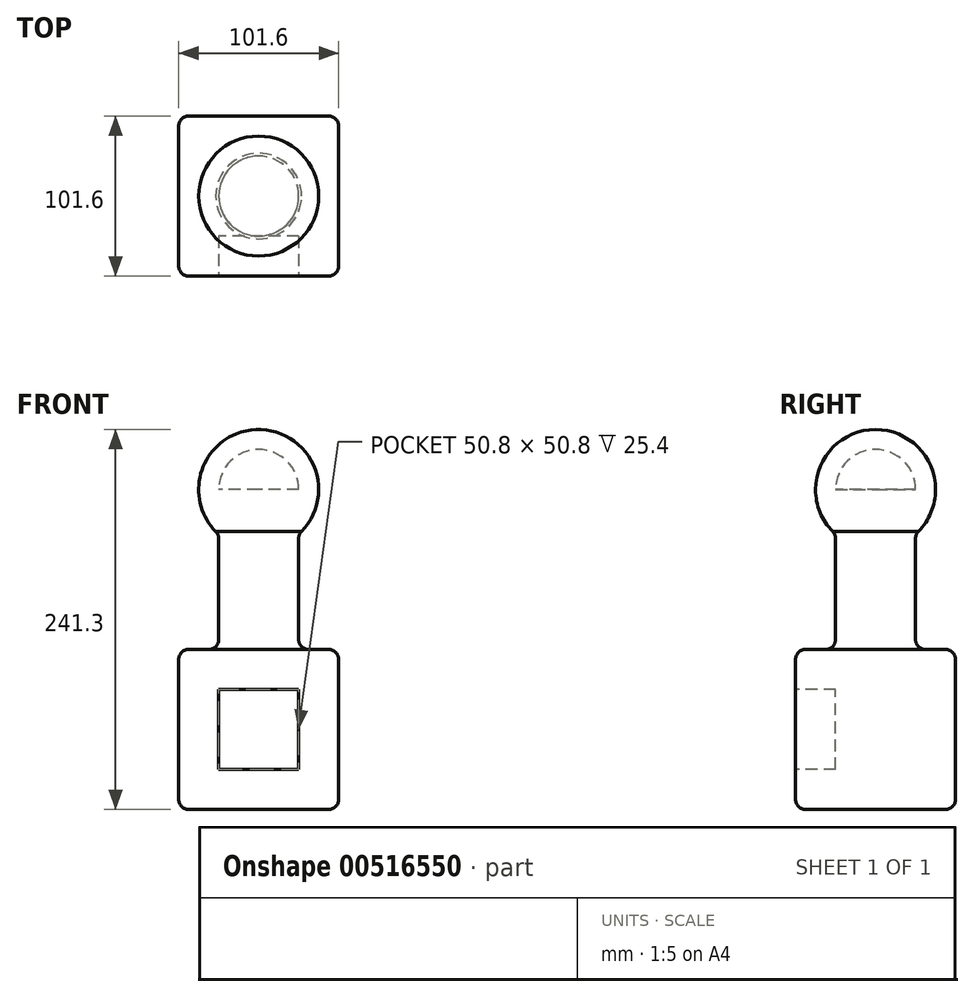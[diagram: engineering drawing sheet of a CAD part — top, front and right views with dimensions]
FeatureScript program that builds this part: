
annotation { "Feature Type Name" : "Feature", "Feature Type Description" : "" }
export const myFeature = defineFeature(function(context is Context, id is Id, definition is map)
    precondition{}
    {
        {
            var Q0;
            Q0=qCreatedBy(makeId("Top.planeOp"),FACE);
            var sketch = newSketch(context, id + "F0", { "sketchPlane" : qUnion([Q0])});
            skLineSegment(sketch, "E0.bottom", {"start": v(-50.8, 50.8) * mm, "end": v(50.8, 50.8) * mm});
            skLineSegment(sketch, "E0.top", {"start": v(-50.8, -50.8) * mm, "end": v(50.8, -50.8) * mm});
            skLineSegment(sketch, "E0.left", {"start": v(-50.8, 50.8) * mm, "end": v(-50.8, -50.8) * mm});
            skLineSegment(sketch, "E0.right", {"start": v(50.8, 50.8) * mm, "end": v(50.8, -50.8) * mm});
            skPoint(sketch, "E0.middle", {"position": v(0, 0) * mm});
            skSolve(sketch);
        }
        {
            var Q0;
            Q0=makeQuery(id+"F0.imprint","IMPRINT",FACE,{"disambiguationData":[TD([[makeQuery(id+"F0.imprint","IMPRINT",EDGE,{"derivedFrom":sQuery(id+"F0.wireOp",EDGE,"E0.bottom")}),-1.0]])]});
            extrude(context, id + "F1", {"entities" : qUnion([Q0]), "depth" : 101.6 * mm, "offsetDistance" : 25.4 * mm});
        }
        {
            var Q0;
            Q0=makeQuery(id+"F1.opExtrude","CAP_FACE",FACE,{"disambiguationData":[OSD([sQuery(id+"F0.wireOp",EDGE,"E0.bottom"),sQuery(id+"F0.wireOp",EDGE,"E0.top"),sQuery(id+"F0.wireOp",EDGE,"E0.left"),sQuery(id+"F0.wireOp",EDGE,"E0.right")])],"isStart":false});
            var sketch = newSketch(context, id + "F2", { "sketchPlane" : qUnion([Q0])});
            skCircle(sketch, "E1", {"center": v(0, 0) * mm, "radius": 25.4 * mm});
            skSolve(sketch);
        }
        {
            var Q0;
            Q0 = qSketchRegion(id + "F2", true);
            extrude(context, id + "F3", {"entities" : qUnion([Q0]), "operationType" : NewBodyOperationType.ADD, "depth" : 101.6 * mm, "offsetDistance" : 25.4 * mm});
        }
        {
            var Q0;
            Q0=makeQuery(id+"F1.opExtrude","SWEPT_FACE",FACE,{"disambiguationData":[OSD([sQuery(id+"F0.wireOp",EDGE,"E0.top")])]});
            var sketch = newSketch(context, id + "F4", { "sketchPlane" : qUnion([Q0])});
            skLineSegment(sketch, "E2.bottom", {"start": v(25.4, 25.4) * mm, "end": v(-25.4, 25.4) * mm});
            skLineSegment(sketch, "E2.top", {"start": v(25.4, 76.2) * mm, "end": v(-25.4, 76.2) * mm});
            skLineSegment(sketch, "E2.left", {"start": v(25.4, 25.4) * mm, "end": v(25.4, 76.2) * mm});
            skLineSegment(sketch, "E2.right", {"start": v(-25.4, 25.4) * mm, "end": v(-25.4, 76.2) * mm});
            skPoint(sketch, "E2.middle", {"position": v(0, 50.8) * mm});
            skPoint(sketch, "E2.middle.positionSnap0", {"position": v(50.8, 50.8) * mm});
            skPoint(sketch, "E2.centerSnap0", {"position": v(50.8, 50.8) * mm});
            skSolve(sketch);
        }
        {
            var Q0;
            Q0=makeQuery(id+"F4.imprint","IMPRINT",FACE,{"disambiguationData":[TD([[makeQuery(id+"F4.imprint","IMPRINT",EDGE,{"derivedFrom":sQuery(id+"F4.wireOp",EDGE,"E2.bottom")}),-1.0]])]});
            extrude(context, id + "F5", {"entities" : qUnion([Q0]), "operationType" : NewBodyOperationType.REMOVE, "oppositeDirection" : true, "depth" : 25.4 * mm, "offsetDistance" : 25.4 * mm});
        }
        {
            var Q0;
            Q0=makeQuery(id+"F3.opExtrude","CAP_FACE",FACE,{"disambiguationData":[OSD([sQuery(id+"F2.wireOp",EDGE,"E1")])],"isStart":false});
            var sketch = newSketch(context, id + "F6", { "sketchPlane" : qUnion([Q0])});
            skArc(sketch, "E3", {"start": v(0, -38.1) * mm, "mid": v(38.1, 0) * mm, "end": v(0, 38.1) * mm});
            skLineSegment(sketch, "E4", {"start": v(0, 38.1) * mm, "end": v(0, -38.1) * mm});
            skSolve(sketch);
        }
        {
            var Q0;
            {var subQ0=sQuery(id+"F6.wireOp",EDGE,"E3");Q0=makeQuery(id+"F6.imprint","IMPRINT",FACE,{"disambiguationData":[TD([[makeQuery(id+"F6.imprint","IMPRINT",EDGE,{"derivedFrom":subQ0}),1.0]])]});}
            var Q1;
            Q1=sQuery(id+"F6.wireOp",EDGE,"E4");
            revolve(context, id + "F7", {"operationType" : NewBodyOperationType.ADD, "entities" : qUnion([Q0]), "axis" : qUnion([Q1]), "revolveType" : RevolveType.FULL});
        }
        {
            var Q0;
            Q0=makeQuery(id+"F1.opExtrude","CAP_EDGE",EDGE,{"disambiguationData":[OSD([sQuery(id+"F0.wireOp",EDGE,"E0.top")])],"isStart":false});
            var Q1;
            Q1=makeQuery(id+"F1.opExtrude","CAP_EDGE",EDGE,{"disambiguationData":[OSD([sQuery(id+"F0.wireOp",EDGE,"E0.left")])],"isStart":false});
            var Q2;
            Q2=makeQuery(id+"F1.opExtrude","CAP_EDGE",EDGE,{"disambiguationData":[OSD([sQuery(id+"F0.wireOp",EDGE,"E0.bottom")])],"isStart":false});
            var Q3;
            Q3=makeQuery(id+"F1.opExtrude","CAP_EDGE",EDGE,{"disambiguationData":[OSD([sQuery(id+"F0.wireOp",EDGE,"E0.right")])],"isStart":false});
            var Q4;
            Q4=makeQuery(id+"F1.opExtrude","SWEPT_EDGE",EDGE,{"disambiguationData":[OSD([sQuery(id+"F0.wireOp",EDGE,"E0.top"),sQuery(id+"F0.wireOp",EDGE,"E0.right")])]});
            var Q5;
            Q5=makeQuery(id+"F1.opExtrude","SWEPT_EDGE",EDGE,{"disambiguationData":[OSD([sQuery(id+"F0.wireOp",EDGE,"E0.top"),sQuery(id+"F0.wireOp",EDGE,"E0.left")])]});
            var Q6;
            Q6=makeQuery(id+"F1.opExtrude","CAP_EDGE",EDGE,{"disambiguationData":[OSD([sQuery(id+"F0.wireOp",EDGE,"E0.right")])],"isStart":true});
            var Q7;
            Q7=makeQuery(id+"F1.opExtrude","CAP_EDGE",EDGE,{"disambiguationData":[OSD([sQuery(id+"F0.wireOp",EDGE,"E0.top")])],"isStart":true});
            var Q8;
            Q8=makeQuery(id+"F1.opExtrude","SWEPT_EDGE",EDGE,{"disambiguationData":[OSD([sQuery(id+"F0.wireOp",EDGE,"E0.bottom"),sQuery(id+"F0.wireOp",EDGE,"E0.right")])]});
            var Q9;
            Q9=makeQuery(id+"F7.boolean.opBoolean","INTERSECT",EDGE,{"derivedFrom":[makeQuery(id+"F3.opExtrude","SWEPT_FACE",FACE,{"disambiguationData":[OSD([sQuery(id+"F2.wireOp",EDGE,"E1")])]}),makeQuery(id+"F7.opRevolve","SWEPT_FACE",FACE,{"disambiguationData":[OSD([sQuery(id+"F6.wireOp",EDGE,"E3")])]})]});
            var Q10;
            Q10=makeQuery(id+"F3.opExtrude","SWEPT_FACE",FACE,{"disambiguationData":[OSD([sQuery(id+"F2.wireOp",EDGE,"E1")])]});
            var Q11;
            Q11=makeQuery(id+"F1.opExtrude","SWEPT_EDGE",EDGE,{"disambiguationData":[OSD([sQuery(id+"F0.wireOp",EDGE,"E0.bottom"),sQuery(id+"F0.wireOp",EDGE,"E0.left")])]});
            var Q12;
            Q12=makeQuery(id+"F1.opExtrude","CAP_EDGE",EDGE,{"disambiguationData":[OSD([sQuery(id+"F0.wireOp",EDGE,"E0.left")])],"isStart":true});
            var Q13;
            Q13=makeQuery(id+"F1.opExtrude","CAP_EDGE",EDGE,{"disambiguationData":[OSD([sQuery(id+"F0.wireOp",EDGE,"E0.bottom")])],"isStart":true});
            fillet(context, id + "F8", {"entities" : qUnion([Q0, Q1, Q2, Q3, Q4, Q5, Q6, Q7, Q8, Q9, Q10, Q11, Q12, Q13]), "radius" : 6.35 * mm, "tangentPropagation" : true, "allowEdgeOverflow" : false});
        }
    });
